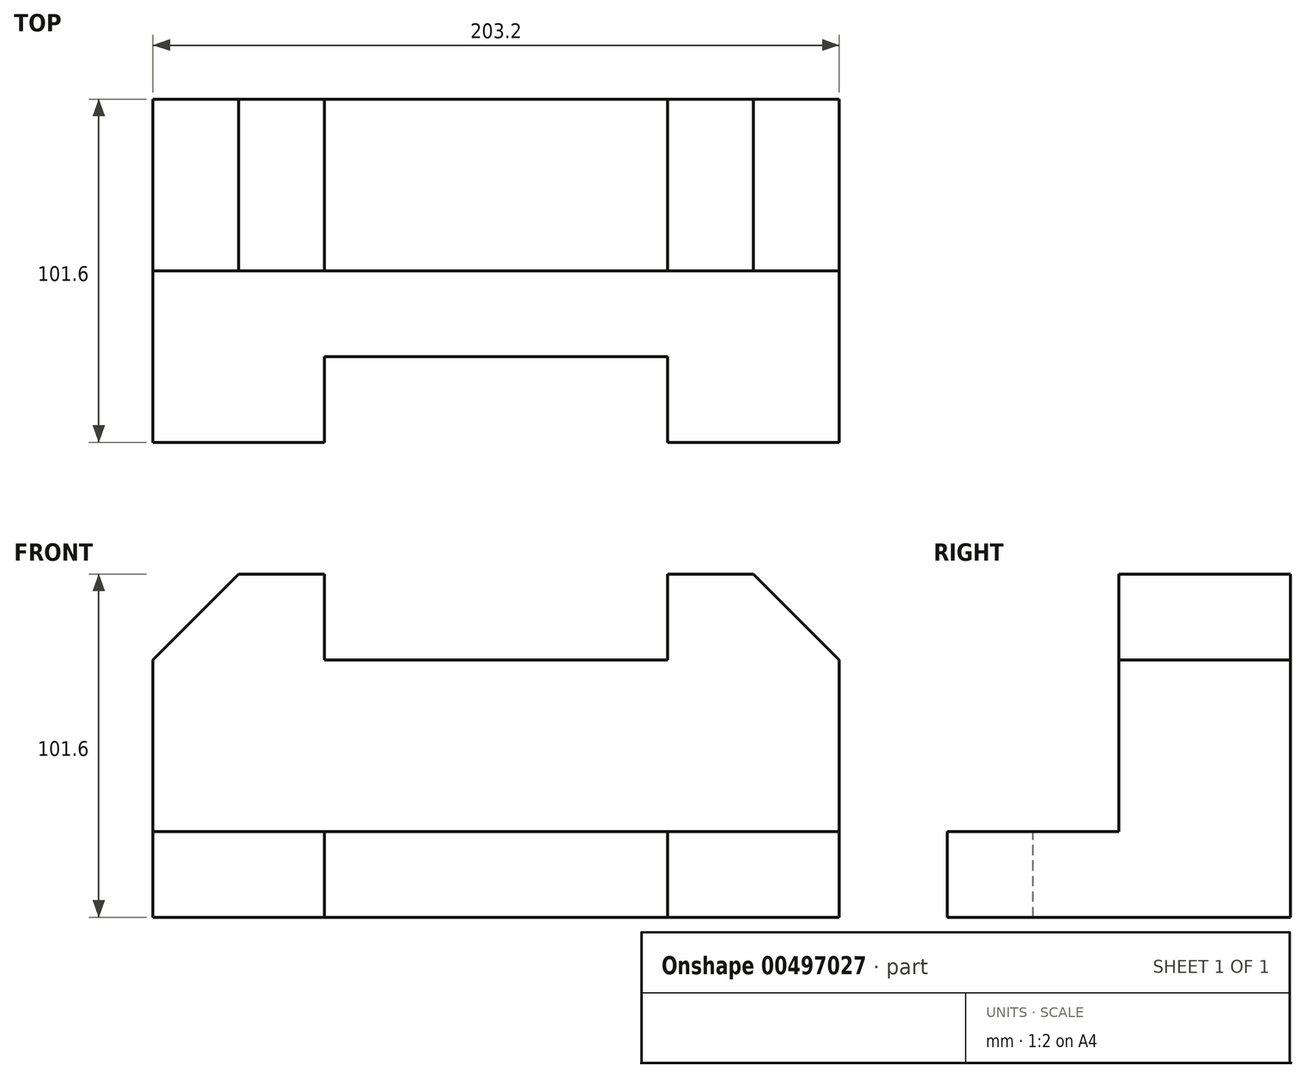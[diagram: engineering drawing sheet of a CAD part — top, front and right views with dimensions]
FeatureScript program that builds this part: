
annotation { "Feature Type Name" : "Feature", "Feature Type Description" : "" }
export const myFeature = defineFeature(function(context is Context, id is Id, definition is map)
    precondition{}
    {
        {
            var Q0;
            Q0=qCreatedBy(makeId("Front.planeOp"),FACE);
            var sketch = newSketch(context, id + "F0", { "sketchPlane" : qUnion([Q0])});
            skLineSegment(sketch, "E0.bottom", {"start": v(0, 0) * mm, "end": v(203.2, 0) * mm});
            skLineSegment(sketch, "E0.top", {"start": v(0, 101.6) * mm, "end": v(50.8, 101.6) * mm});
            skLineSegment(sketch, "E0.left", {"start": v(0, 0) * mm, "end": v(0, 101.6) * mm});
            skLineSegment(sketch, "E0.right", {"start": v(203.2, 0) * mm, "end": v(203.2, 101.6) * mm});
            skLineSegment(sketch, "E1", {"start": v(50.8, 101.6) * mm, "end": v(50.8, 76.2) * mm});
            skLineSegment(sketch, "E2", {"start": v(50.8, 76.2) * mm, "end": v(0, 76.2) * mm});
            skLineSegment(sketch, "E3", {"start": v(152.4, 101.6) * mm, "end": v(152.4, 76.2) * mm});
            skLineSegment(sketch, "E4", {"start": v(152.4, 76.2) * mm, "end": v(203.2, 76.2) * mm});
            skLineSegment(sketch, "E5", {"start": v(50.8, 76.2) * mm, "end": v(152.4, 76.2) * mm});
            skLineSegment(sketch, "E6.trimOffspring", {"start": v(152.4, 101.6) * mm, "end": v(203.2, 101.6) * mm});
            skSolve(sketch);
        }
        {
            var Q0;
            Q0 = qSketchRegion(id + "F0", true);
            extrude(context, id + "F1", {"entities" : qUnion([Q0]), "depth" : 50.8 * mm});
        }
        {
            var Q0;
            Q0=makeQuery(id+"F1.opExtrude","SWEPT_EDGE",EDGE,{"disambiguationData":[OSD([sQuery(id+"F0.wireOp",EDGE,"E0.right"),sQuery(id+"F0.wireOp",EDGE,"E6.trimOffspring")])]});
            chamfer(context, id + "F2", {"entities" : qUnion([Q0]), "width" : 25.4 * mm, "tangentPropagation" : true});
        }
        {
            var Q0;
            Q0=makeQuery(id+"F1.opExtrude","SWEPT_EDGE",EDGE,{"disambiguationData":[OSD([sQuery(id+"F0.wireOp",EDGE,"E0.top"),sQuery(id+"F0.wireOp",EDGE,"E0.left")])]});
            chamfer(context, id + "F3", {"entities" : qUnion([Q0]), "width" : 25.4 * mm, "tangentPropagation" : true});
        }
        {
            var Q0;
            Q0=makeQuery(id+"F1.opExtrude","CAP_FACE",FACE,{"disambiguationData":[OSD([sQuery(id+"F0.wireOp",EDGE,"E0.bottom"),sQuery(id+"F0.wireOp",EDGE,"E0.top"),sQuery(id+"F0.wireOp",EDGE,"E0.left"),sQuery(id+"F0.wireOp",EDGE,"E0.right"),sQuery(id+"F0.wireOp",EDGE,"E1"),sQuery(id+"F0.wireOp",EDGE,"E3"),sQuery(id+"F0.wireOp",EDGE,"E5"),sQuery(id+"F0.wireOp",EDGE,"E6.trimOffspring")])],"isStart":false});
            var sketch = newSketch(context, id + "F4", { "sketchPlane" : qUnion([Q0])});
            skLineSegment(sketch, "E7", {"start": v(0, 25.4) * mm, "end": v(203.2, 25.4) * mm});
            skSolve(sketch);
        }
        {
            var Q0;
            {var subQ0=sQuery(id+"F4.wireOp",EDGE,"E7");Q0=makeQuery(id+"F4.imprint","IMPRINT",FACE,{"disambiguationData":[TD([[makeQuery(id+"F4.imprint","IMPRINT",EDGE,{"derivedFrom":subQ0}),-1.0]])]});}
            extrude(context, id + "F5", {"entities" : qUnion([Q0]), "operationType" : NewBodyOperationType.ADD, "depth" : 50.8 * mm});
        }
        {
            var Q0;
            Q0=makeQuery(id+"F5.opExtrude","SWEPT_FACE",FACE,{"disambiguationData":[OSD([sQuery(id+"F4.wireOp",EDGE,"E7")])]});
            var sketch = newSketch(context, id + "F6", { "sketchPlane" : qUnion([Q0])});
            skLineSegment(sketch, "E8", {"start": v(50.8, -101.6) * mm, "end": v(50.8, -50.8) * mm});
            skLineSegment(sketch, "E9", {"start": v(152.4, -101.6) * mm, "end": v(152.4, -50.8) * mm});
            skLineSegment(sketch, "E10", {"start": v(50.8, -76.2) * mm, "end": v(152.4, -76.2) * mm});
            skSolve(sketch);
        }
        {
            var Q0;
            {var subQ3=sQuery(id+"F6.wireOp",EDGE,"E10");Q0=makeQuery(id+"F6.imprint","IMPRINT",FACE,{"disambiguationData":[TD([[makeQuery(id+"F6.imprint","IMPRINT",EDGE,{"derivedFrom":subQ3}),-1.0]])]});}
            extrude(context, id + "F7", {"entities" : qUnion([Q0]), "operationType" : NewBodyOperationType.REMOVE, "oppositeDirection" : true, "depth" : 25.4 * mm});
        }
    });
